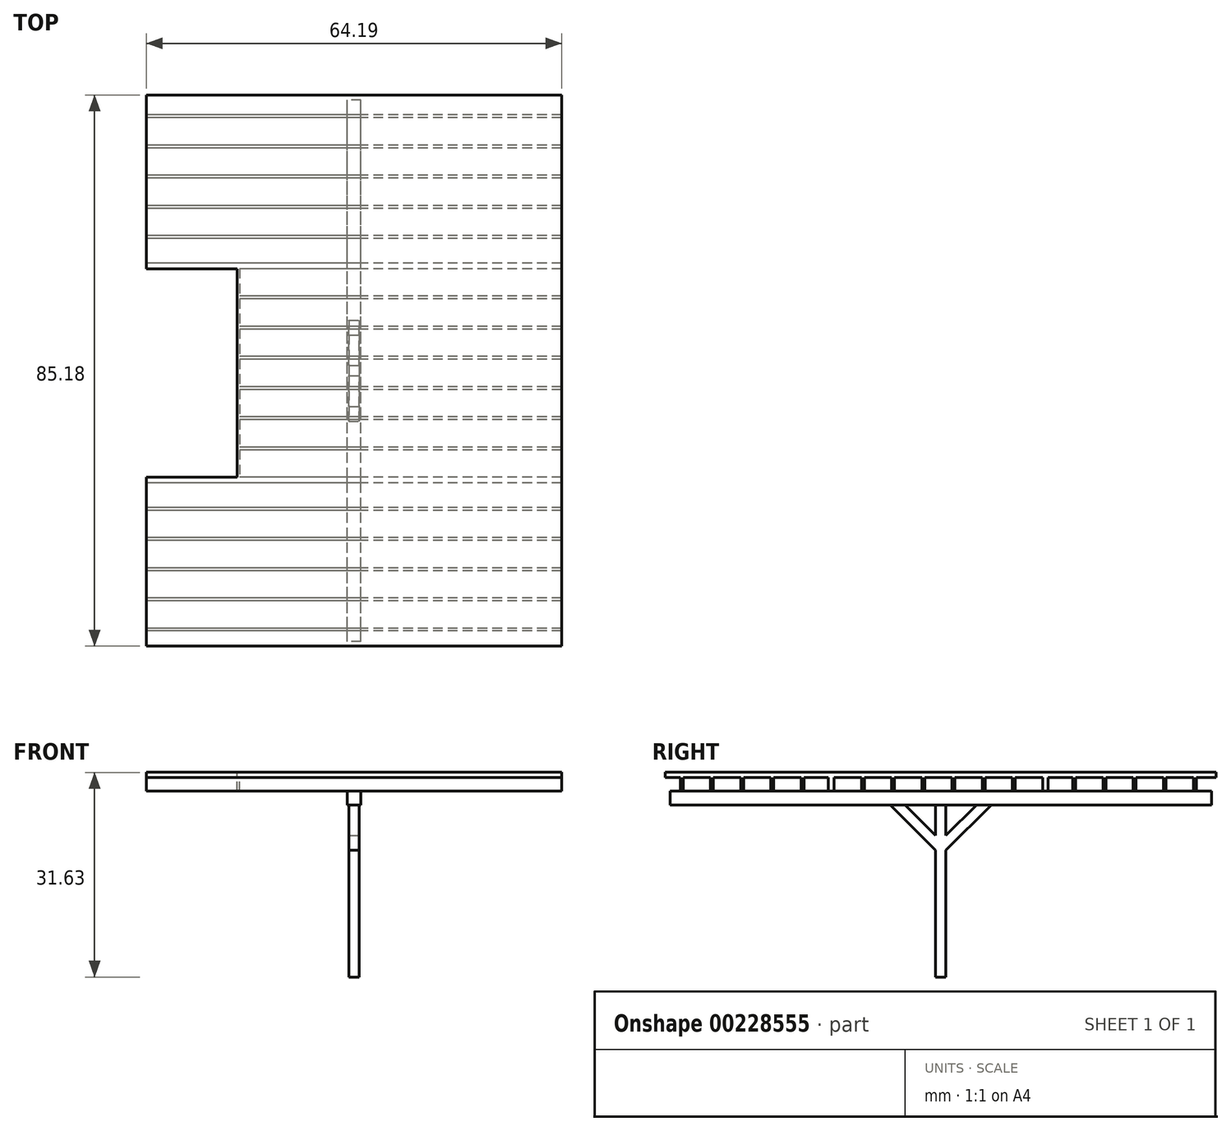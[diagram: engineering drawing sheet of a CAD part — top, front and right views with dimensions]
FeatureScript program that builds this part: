
annotation { "Feature Type Name" : "Feature", "Feature Type Description" : "" }
export const myFeature = defineFeature(function(context is Context, id is Id, definition is map)
    precondition{}
    {
        {
            var Q0;
            Q0=qCreatedBy(makeId("Top.planeOp"),FACE);
            var sketch = newSketch(context, id + "F0", { "sketchPlane" : qUnion([Q0])});
            skLineSegment(sketch, "E0.bottom", {"start": v(-4.2, 0) * mm, "end": v(5863.2, 0) * mm});
            skLineSegment(sketch, "E0.top", {"start": v(-4.2, -7696.2) * mm, "end": v(5863.2, -7696.2) * mm});
            skLineSegment(sketch, "E0.left", {"start": v(-4.2, 0) * mm, "end": v(-4.2, -7696.2) * mm});
            skLineSegment(sketch, "E0.right", {"start": v(5863.2, 0) * mm, "end": v(5863.2, -7696.2) * mm});
            skSolve(sketch);
        }
        {
            var Q0;
            Q0=makeQuery(id+"F0.imprint","IMPRINT",FACE,{"disambiguationData":[TD([[makeQuery(id+"F0.imprint","IMPRINT",EDGE,{"derivedFrom":sQuery(id+"F0.wireOp",EDGE,"E0.bottom")}),-1.0]])]});
            extrude(context, id + "F1", {"entities" : qUnion([Q0]), "depth" : 69.14 * mm});
        }
        {
            var Q0;
            Q0=makeQuery(id+"F1.opExtrude","CAP_FACE",FACE,{"disambiguationData":[OSD([sQuery(id+"F0.wireOp",EDGE,"E0.bottom"),sQuery(id+"F0.wireOp",EDGE,"E0.top"),sQuery(id+"F0.wireOp",EDGE,"E0.left"),sQuery(id+"F0.wireOp",EDGE,"E0.right")])],"isStart":true});
            var sketch = newSketch(context, id + "F2", { "sketchPlane" : qUnion([Q0])});
            skLineSegment(sketch, "E1.0", {"start": v(33.9, 7658.1) * mm, "end": v(5825.1, 7658.1) * mm});
            skLineSegment(sketch, "E1.1", {"start": v(33.9, 38.1) * mm, "end": v(33.9, 7658.1) * mm});
            skLineSegment(sketch, "E1.2", {"start": v(33.9, 38.1) * mm, "end": v(5825.1, 38.1) * mm});
            skLineSegment(sketch, "E1.3", {"start": v(5825.1, 38.1) * mm, "end": v(5825.1, 7658.1) * mm});
            skSolve(sketch);
        }
        {
            var Q0;
            Q0=makeQuery(id+"F2.imprint","IMPRINT",FACE,{"disambiguationData":[TD([[makeQuery(id+"F2.imprint","IMPRINT",EDGE,{"derivedFrom":sQuery(id+"F2.wireOp",EDGE,"E1.0")}),1.0]])]});
            extrude(context, id + "F3", {"entities" : qUnion([Q0]), "operationType" : NewBodyOperationType.ADD, "depth" : 184.15 * mm});
        }
        {
            var Q0;
            Q0=qCreatedBy(makeId("Right.planeOp"),FACE);
            var sketch = newSketch(context, id + "F4", { "sketchPlane" : qUnion([Q0])});
            skLineSegment(sketch, "E2.bottom", {"start": v(-406.4, 0) * mm, "end": v(-444.5, 0) * mm});
            skLineSegment(sketch, "E2.top", {"start": v(-406.4, -184.15) * mm, "end": v(-444.5, -184.15) * mm});
            skLineSegment(sketch, "E2.left", {"start": v(-406.4, 0) * mm, "end": v(-406.4, -184.15) * mm});
            skLineSegment(sketch, "E2.right", {"start": v(-444.5, 0) * mm, "end": v(-444.5, -184.15) * mm});
            skLineSegment(sketch, "E3.1.0.0", {"start": v(-812.8, 0) * mm, "end": v(-812.8, -184.15) * mm});
            skLineSegment(sketch, "E3.1.0.1", {"start": v(-850.9, 0) * mm, "end": v(-850.9, -184.15) * mm});
            skLineSegment(sketch, "E3.1.0.2", {"start": v(-812.8, 0) * mm, "end": v(-850.9, 0) * mm});
            skLineSegment(sketch, "E3.1.0.3", {"start": v(-812.8, -184.15) * mm, "end": v(-850.9, -184.15) * mm});
            skLineSegment(sketch, "E3.2.0.0", {"start": v(-1219.2, 0) * mm, "end": v(-1219.2, -184.15) * mm});
            skLineSegment(sketch, "E3.2.0.1", {"start": v(-1257.3, 0) * mm, "end": v(-1257.3, -184.15) * mm});
            skLineSegment(sketch, "E3.2.0.2", {"start": v(-1219.2, 0) * mm, "end": v(-1257.3, 0) * mm});
            skLineSegment(sketch, "E3.2.0.3", {"start": v(-1219.2, -184.15) * mm, "end": v(-1257.3, -184.15) * mm});
            skLineSegment(sketch, "E3.3.0.0", {"start": v(-1625.6, 0) * mm, "end": v(-1625.6, -184.15) * mm});
            skLineSegment(sketch, "E3.3.0.1", {"start": v(-1663.7, 0) * mm, "end": v(-1663.7, -184.15) * mm});
            skLineSegment(sketch, "E3.3.0.2", {"start": v(-1625.6, 0) * mm, "end": v(-1663.7, 0) * mm});
            skLineSegment(sketch, "E3.3.0.3", {"start": v(-1625.6, -184.15) * mm, "end": v(-1663.7, -184.15) * mm});
            skLineSegment(sketch, "E3.4.0.0", {"start": v(-2032, 0) * mm, "end": v(-2032, -184.15) * mm});
            skLineSegment(sketch, "E3.4.0.1", {"start": v(-2070.1, 0) * mm, "end": v(-2070.1, -184.15) * mm});
            skLineSegment(sketch, "E3.4.0.2", {"start": v(-2032, 0) * mm, "end": v(-2070.1, 0) * mm});
            skLineSegment(sketch, "E3.4.0.3", {"start": v(-2032, -184.15) * mm, "end": v(-2070.1, -184.15) * mm});
            skLineSegment(sketch, "E3.5.0.0", {"start": v(-2438.4, 0) * mm, "end": v(-2438.4, -184.15) * mm});
            skLineSegment(sketch, "E3.5.0.1", {"start": v(-2476.5, 0) * mm, "end": v(-2476.5, -184.15) * mm});
            skLineSegment(sketch, "E3.5.0.2", {"start": v(-2438.4, 0) * mm, "end": v(-2476.5, 0) * mm});
            skLineSegment(sketch, "E3.5.0.3", {"start": v(-2438.4, -184.15) * mm, "end": v(-2476.5, -184.15) * mm});
            skLineSegment(sketch, "E3.6.0.0", {"start": v(-2844.8, 0) * mm, "end": v(-2844.8, -184.15) * mm});
            skLineSegment(sketch, "E3.6.0.1", {"start": v(-2882.9, 0) * mm, "end": v(-2882.9, -184.15) * mm});
            skLineSegment(sketch, "E3.6.0.2", {"start": v(-2844.8, 0) * mm, "end": v(-2882.9, 0) * mm});
            skLineSegment(sketch, "E3.6.0.3", {"start": v(-2844.8, -184.15) * mm, "end": v(-2882.9, -184.15) * mm});
            skLineSegment(sketch, "E3.7.0.0", {"start": v(-3251.2, 0) * mm, "end": v(-3251.2, -184.15) * mm});
            skLineSegment(sketch, "E3.7.0.1", {"start": v(-3289.3, 0) * mm, "end": v(-3289.3, -184.15) * mm});
            skLineSegment(sketch, "E3.7.0.2", {"start": v(-3251.2, 0) * mm, "end": v(-3289.3, 0) * mm});
            skLineSegment(sketch, "E3.7.0.3", {"start": v(-3251.2, -184.15) * mm, "end": v(-3289.3, -184.15) * mm});
            skLineSegment(sketch, "E3.8.0.0", {"start": v(-3657.6, 0) * mm, "end": v(-3657.6, -184.15) * mm});
            skLineSegment(sketch, "E3.8.0.1", {"start": v(-3695.7, 0) * mm, "end": v(-3695.7, -184.15) * mm});
            skLineSegment(sketch, "E3.8.0.2", {"start": v(-3657.6, 0) * mm, "end": v(-3695.7, 0) * mm});
            skLineSegment(sketch, "E3.8.0.3", {"start": v(-3657.6, -184.15) * mm, "end": v(-3695.7, -184.15) * mm});
            skLineSegment(sketch, "E3.9.0.0", {"start": v(-4064, 0) * mm, "end": v(-4064, -184.15) * mm});
            skLineSegment(sketch, "E3.9.0.1", {"start": v(-4102.1, 0) * mm, "end": v(-4102.1, -184.15) * mm});
            skLineSegment(sketch, "E3.9.0.2", {"start": v(-4064, 0) * mm, "end": v(-4102.1, 0) * mm});
            skLineSegment(sketch, "E3.9.0.3", {"start": v(-4064, -184.15) * mm, "end": v(-4102.1, -184.15) * mm});
            skLineSegment(sketch, "E3.10.0.0", {"start": v(-4470.4, 0) * mm, "end": v(-4470.4, -184.15) * mm});
            skLineSegment(sketch, "E3.10.0.1", {"start": v(-4508.5, 0) * mm, "end": v(-4508.5, -184.15) * mm});
            skLineSegment(sketch, "E3.10.0.2", {"start": v(-4470.4, 0) * mm, "end": v(-4508.5, 0) * mm});
            skLineSegment(sketch, "E3.10.0.3", {"start": v(-4470.4, -184.15) * mm, "end": v(-4508.5, -184.15) * mm});
            skLineSegment(sketch, "E3.11.0.0", {"start": v(-4876.8, 0) * mm, "end": v(-4876.8, -184.15) * mm});
            skLineSegment(sketch, "E3.11.0.1", {"start": v(-4914.9, 0) * mm, "end": v(-4914.9, -184.15) * mm});
            skLineSegment(sketch, "E3.11.0.2", {"start": v(-4876.8, 0) * mm, "end": v(-4914.9, 0) * mm});
            skLineSegment(sketch, "E3.11.0.3", {"start": v(-4876.8, -184.15) * mm, "end": v(-4914.9, -184.15) * mm});
            skLineSegment(sketch, "E3.12.0.0", {"start": v(-5283.2, 0) * mm, "end": v(-5283.2, -184.15) * mm});
            skLineSegment(sketch, "E3.12.0.1", {"start": v(-5321.3, 0) * mm, "end": v(-5321.3, -184.15) * mm});
            skLineSegment(sketch, "E3.12.0.2", {"start": v(-5283.2, 0) * mm, "end": v(-5321.3, 0) * mm});
            skLineSegment(sketch, "E3.12.0.3", {"start": v(-5283.2, -184.15) * mm, "end": v(-5321.3, -184.15) * mm});
            skLineSegment(sketch, "E3.13.0.0", {"start": v(-5689.6, 0) * mm, "end": v(-5689.6, -184.15) * mm});
            skLineSegment(sketch, "E3.13.0.1", {"start": v(-5727.7, 0) * mm, "end": v(-5727.7, -184.15) * mm});
            skLineSegment(sketch, "E3.13.0.2", {"start": v(-5689.6, 0) * mm, "end": v(-5727.7, 0) * mm});
            skLineSegment(sketch, "E3.13.0.3", {"start": v(-5689.6, -184.15) * mm, "end": v(-5727.7, -184.15) * mm});
            skLineSegment(sketch, "E3.14.0.0", {"start": v(-6096, 0) * mm, "end": v(-6096, -184.15) * mm});
            skLineSegment(sketch, "E3.14.0.1", {"start": v(-6134.1, 0) * mm, "end": v(-6134.1, -184.15) * mm});
            skLineSegment(sketch, "E3.14.0.2", {"start": v(-6096, 0) * mm, "end": v(-6134.1, 0) * mm});
            skLineSegment(sketch, "E3.14.0.3", {"start": v(-6096, -184.15) * mm, "end": v(-6134.1, -184.15) * mm});
            skLineSegment(sketch, "E3.15.0.0", {"start": v(-6502.4, 0) * mm, "end": v(-6502.4, -184.15) * mm});
            skLineSegment(sketch, "E3.15.0.1", {"start": v(-6540.5, 0) * mm, "end": v(-6540.5, -184.15) * mm});
            skLineSegment(sketch, "E3.15.0.2", {"start": v(-6502.4, 0) * mm, "end": v(-6540.5, 0) * mm});
            skLineSegment(sketch, "E3.15.0.3", {"start": v(-6502.4, -184.15) * mm, "end": v(-6540.5, -184.15) * mm});
            skLineSegment(sketch, "E3.16.0.0", {"start": v(-6908.8, 0) * mm, "end": v(-6908.8, -184.15) * mm});
            skLineSegment(sketch, "E3.16.0.1", {"start": v(-6946.9, 0) * mm, "end": v(-6946.9, -184.15) * mm});
            skLineSegment(sketch, "E3.16.0.2", {"start": v(-6908.8, 0) * mm, "end": v(-6946.9, 0) * mm});
            skLineSegment(sketch, "E3.16.0.3", {"start": v(-6908.8, -184.15) * mm, "end": v(-6946.9, -184.15) * mm});
            skLineSegment(sketch, "E3.direction1", {"start": v(-444.5, -184.15) * mm, "end": v(-850.9, -184.15) * mm, "construction": true});
            skLineSegment(sketch, "E4.0.17.0", {"start": v(-7315.2, 0) * mm, "end": v(-7315.2, -184.15) * mm});
            skLineSegment(sketch, "E4.3.17.0", {"start": v(-7353.3, 0) * mm, "end": v(-7353.3, -184.15) * mm});
            skLineSegment(sketch, "E4.6.17.0", {"start": v(-7315.2, 0) * mm, "end": v(-7353.3, 0) * mm});
            skLineSegment(sketch, "E4.9.17.0", {"start": v(-7315.2, -184.15) * mm, "end": v(-7353.3, -184.15) * mm});
            skSolve(sketch);
        }
        {
            var Q0;
            Q0=makeQuery(id+"F4.imprint","IMPRINT",FACE,{"disambiguationData":[TD([[makeQuery(id+"F4.imprint","IMPRINT",EDGE,{"derivedFrom":sQuery(id+"F4.wireOp",EDGE,"E2.bottom")}),1.0]])]});
            var Q1;
            Q1=makeQuery(id+"F4.imprint","IMPRINT",FACE,{"disambiguationData":[TD([[makeQuery(id+"F4.imprint","IMPRINT",EDGE,{"derivedFrom":sQuery(id+"F4.wireOp",EDGE,"E3.1.0.0")}),-1.0]])]});
            var Q2;
            Q2=makeQuery(id+"F4.imprint","IMPRINT",FACE,{"disambiguationData":[TD([[makeQuery(id+"F4.imprint","IMPRINT",EDGE,{"derivedFrom":sQuery(id+"F4.wireOp",EDGE,"E3.2.0.0")}),-1.0]])]});
            var Q3;
            Q3=makeQuery(id+"F4.imprint","IMPRINT",FACE,{"disambiguationData":[TD([[makeQuery(id+"F4.imprint","IMPRINT",EDGE,{"derivedFrom":sQuery(id+"F4.wireOp",EDGE,"E3.3.0.0")}),-1.0]])]});
            var Q4;
            Q4=makeQuery(id+"F4.imprint","IMPRINT",FACE,{"disambiguationData":[TD([[makeQuery(id+"F4.imprint","IMPRINT",EDGE,{"derivedFrom":sQuery(id+"F4.wireOp",EDGE,"E3.4.0.0")}),-1.0]])]});
            var Q5;
            Q5=makeQuery(id+"F4.imprint","IMPRINT",FACE,{"disambiguationData":[TD([[makeQuery(id+"F4.imprint","IMPRINT",EDGE,{"derivedFrom":sQuery(id+"F4.wireOp",EDGE,"E3.5.0.0")}),-1.0]])]});
            var Q6;
            Q6=makeQuery(id+"F4.imprint","IMPRINT",FACE,{"disambiguationData":[TD([[makeQuery(id+"F4.imprint","IMPRINT",EDGE,{"derivedFrom":sQuery(id+"F4.wireOp",EDGE,"E3.6.0.0")}),-1.0]])]});
            var Q7;
            Q7=makeQuery(id+"F4.imprint","IMPRINT",FACE,{"disambiguationData":[TD([[makeQuery(id+"F4.imprint","IMPRINT",EDGE,{"derivedFrom":sQuery(id+"F4.wireOp",EDGE,"E3.7.0.0")}),-1.0]])]});
            var Q8;
            Q8=makeQuery(id+"F4.imprint","IMPRINT",FACE,{"disambiguationData":[TD([[makeQuery(id+"F4.imprint","IMPRINT",EDGE,{"derivedFrom":sQuery(id+"F4.wireOp",EDGE,"E3.8.0.0")}),-1.0]])]});
            var Q9;
            Q9=makeQuery(id+"F4.imprint","IMPRINT",FACE,{"disambiguationData":[TD([[makeQuery(id+"F4.imprint","IMPRINT",EDGE,{"derivedFrom":sQuery(id+"F4.wireOp",EDGE,"E3.9.0.0")}),-1.0]])]});
            var Q10;
            Q10=makeQuery(id+"F4.imprint","IMPRINT",FACE,{"disambiguationData":[TD([[makeQuery(id+"F4.imprint","IMPRINT",EDGE,{"derivedFrom":sQuery(id+"F4.wireOp",EDGE,"E3.10.0.0")}),-1.0]])]});
            var Q11;
            Q11=makeQuery(id+"F4.imprint","IMPRINT",FACE,{"disambiguationData":[TD([[makeQuery(id+"F4.imprint","IMPRINT",EDGE,{"derivedFrom":sQuery(id+"F4.wireOp",EDGE,"E3.11.0.0")}),-1.0]])]});
            var Q12;
            Q12=makeQuery(id+"F4.imprint","IMPRINT",FACE,{"disambiguationData":[TD([[makeQuery(id+"F4.imprint","IMPRINT",EDGE,{"derivedFrom":sQuery(id+"F4.wireOp",EDGE,"E3.12.0.0")}),-1.0]])]});
            var Q13;
            Q13=makeQuery(id+"F4.imprint","IMPRINT",FACE,{"disambiguationData":[TD([[makeQuery(id+"F4.imprint","IMPRINT",EDGE,{"derivedFrom":sQuery(id+"F4.wireOp",EDGE,"E3.13.0.0")}),-1.0]])]});
            var Q14;
            Q14=makeQuery(id+"F4.imprint","IMPRINT",FACE,{"disambiguationData":[TD([[makeQuery(id+"F4.imprint","IMPRINT",EDGE,{"derivedFrom":sQuery(id+"F4.wireOp",EDGE,"E3.14.0.0")}),-1.0]])]});
            var Q15;
            Q15=makeQuery(id+"F4.imprint","IMPRINT",FACE,{"disambiguationData":[TD([[makeQuery(id+"F4.imprint","IMPRINT",EDGE,{"derivedFrom":sQuery(id+"F4.wireOp",EDGE,"E3.15.0.0")}),-1.0]])]});
            var Q16;
            Q16=makeQuery(id+"F4.imprint","IMPRINT",FACE,{"disambiguationData":[TD([[makeQuery(id+"F4.imprint","IMPRINT",EDGE,{"derivedFrom":sQuery(id+"F4.wireOp",EDGE,"E3.16.0.0")}),-1.0]])]});
            var Q17;
            Q17=makeQuery(id+"F4.imprint","IMPRINT",FACE,{"disambiguationData":[TD([[makeQuery(id+"F4.imprint","IMPRINT",EDGE,{"derivedFrom":sQuery(id+"F4.wireOp",EDGE,"E4.0.17.0")}),-1.0]])]});
            var Q18;
            Q18=makeQuery(id+"F1.opExtrude","SWEPT_FACE",FACE,{"disambiguationData":[OSD([sQuery(id+"F0.wireOp",EDGE,"E0.right")])]});
            extrude(context, id + "F5", {"entities" : qUnion([Q0, Q1, Q2, Q3, Q4, Q5, Q6, Q7, Q8, Q9, Q10, Q11, Q12, Q13, Q14, Q15, Q16, Q17]), "operationType" : NewBodyOperationType.ADD, "endBound" : BoundingType.UP_TO_SURFACE, "endBoundEntityFace" : qUnion([Q18]), "depth" : 25.4 * mm});
        }
        {
            var Q0;
            {var subQ0=sQuery(id+"F0.wireOp",EDGE,"E0.bottom");Q0=makeQuery(id+"F3.boolean.opBoolean","MERGE",FACE,{"derivedFrom":[makeQuery(id+"F1.opExtrude","SWEPT_FACE",FACE,{"disambiguationData":[OSD([subQ0])]}),makeQuery(id+"F3.opExtrude","SWEPT_FACE",FACE,{"disambiguationData":[OSD([subQ0])]})]});}
            cPlane(context, id + "F6", {"entities" : qUnion([Q0]), "cplaneType" : CPlaneType.OFFSET, "offset" : 203.2 * mm, "oppositeDirection" : true, "width" : 152.4 * mm, "height" : 152.4 * mm});
        }
        {
            var Q0;
            Q0=qCreatedBy(id+"F6.planeOp",FACE);
            var sketch = newSketch(context, id + "F7", { "sketchPlane" : qUnion([Q0])});
            skLineSegment(sketch, "E5.bottom", {"start": v(-3021.58, -184.15) * mm, "end": v(-2837.43, -184.15) * mm});
            skLineSegment(sketch, "E5.top", {"start": v(-3021.58, -368.3) * mm, "end": v(-2837.43, -368.3) * mm});
            skLineSegment(sketch, "E5.left", {"start": v(-3021.58, -184.15) * mm, "end": v(-3021.58, -368.3) * mm});
            skLineSegment(sketch, "E5.right", {"start": v(-2837.43, -184.15) * mm, "end": v(-2837.43, -368.3) * mm});
            skSolve(sketch);
        }
        {
            var Q0;
            Q0=makeQuery(id+"F7.imprint","IMPRINT",FACE,{"disambiguationData":[TD([[makeQuery(id+"F7.imprint","IMPRINT",EDGE,{"derivedFrom":sQuery(id+"F7.wireOp",EDGE,"E5.bottom")}),-1.0]])]});
            extrude(context, id + "F8", {"entities" : qUnion([Q0]), "operationType" : NewBodyOperationType.ADD, "oppositeDirection" : true, "depth" : 7289.8 * mm});
        }
        {
            var Q0;
            Q0=makeQuery(id+"F8.opExtrude","SWEPT_FACE",FACE,{"disambiguationData":[OSD([sQuery(id+"F7.wireOp",EDGE,"E5.top")])]});
            var sketch = newSketch(context, id + "F9", { "sketchPlane" : qUnion([Q0])});
            skLineSegment(sketch, "E6", {"start": v(2929.5, 7493) * mm, "end": v(2929.5, 203.2) * mm, "construction": true});
            skLineSegment(sketch, "E7", {"start": v(2837.43, 3848.1) * mm, "end": v(3021.58, 3848.1) * mm, "construction": true});
            skLineSegment(sketch, "E8.bottom", {"start": v(2999.36, 3778.25) * mm, "end": v(2859.66, 3778.25) * mm});
            skLineSegment(sketch, "E8.top", {"start": v(2999.36, 3917.95) * mm, "end": v(2859.66, 3917.95) * mm});
            skLineSegment(sketch, "E8.left", {"start": v(2999.36, 3778.25) * mm, "end": v(2999.36, 3917.95) * mm});
            skLineSegment(sketch, "E8.right", {"start": v(2859.66, 3778.25) * mm, "end": v(2859.66, 3917.95) * mm});
            skPoint(sketch, "E8.middle", {"position": v(2929.5, 3848.1) * mm});
            skSolve(sketch);
        }
        {
            var Q0;
            Q0=makeQuery(id+"F9.imprint","IMPRINT",FACE,{"disambiguationData":[TD([[makeQuery(id+"F9.imprint","IMPRINT",EDGE,{"derivedFrom":sQuery(id+"F9.wireOp",EDGE,"E8.bottom")}),-1.0]])]});
            extrude(context, id + "F10", {"entities" : qUnion([Q0]), "operationType" : NewBodyOperationType.ADD, "depth" : 2317.62 * mm});
        }
        {
            var Q0;
            Q0=makeQuery(id+"F10.opExtrude","SWEPT_FACE",FACE,{"disambiguationData":[OSD([sQuery(id+"F9.wireOp",EDGE,"E8.left")])]});
            var sketch = newSketch(context, id + "F11", { "sketchPlane" : qUnion([Q0])});
            skLineSegment(sketch, "E9", {"start": v(-4329.98, -368.3) * mm, "end": v(-3917.95, -780.33) * mm});
            skLineSegment(sketch, "E10", {"start": v(-3917.95, -780.33) * mm, "end": v(-3917.95, -977.9) * mm});
            skLineSegment(sketch, "E11", {"start": v(-3917.95, -977.9) * mm, "end": v(-4527.55, -368.3) * mm});
            skLineSegment(sketch, "E12", {"start": v(-4527.55, -368.3) * mm, "end": v(-4329.98, -368.3) * mm});
            skLineSegment(sketch, "E13", {"start": v(-3848.1, -1904.76) * mm, "end": v(-3848.1, -2685.92) * mm, "construction": true});
            skLineSegment(sketch, "E14.MirrorCS", {"start": v(-3168.65, -368.3) * mm, "end": v(-3366.22, -368.3) * mm});
            skLineSegment(sketch, "E15.MirrorCS", {"start": v(-3778.25, -977.9) * mm, "end": v(-3168.65, -368.3) * mm});
            skLineSegment(sketch, "E16.MirrorCS", {"start": v(-3366.22, -368.3) * mm, "end": v(-3778.25, -780.33) * mm});
            skLineSegment(sketch, "E17.MirrorCS", {"start": v(-3778.25, -780.33) * mm, "end": v(-3778.25, -977.9) * mm});
            skSolve(sketch);
        }
        {
            var Q0;
            Q0=makeQuery(id+"F11.imprint","IMPRINT",FACE,{"disambiguationData":[TD([[makeQuery(id+"F11.imprint","IMPRINT",EDGE,{"derivedFrom":sQuery(id+"F11.wireOp",EDGE,"E9")}),-1.0]])]});
            var Q1;
            Q1=makeQuery(id+"F11.imprint","IMPRINT",FACE,{"disambiguationData":[TD([[makeQuery(id+"F11.imprint","IMPRINT",EDGE,{"derivedFrom":sQuery(id+"F11.wireOp",EDGE,"E14.MirrorCS")}),1.0]])]});
            var Q2;
            Q2=makeQuery(id+"F11.imprint","IMPRINT",FACE,{"disambiguationData":[TD([[makeQuery(id+"F11.imprint","IMPRINT",EDGE,{"derivedFrom":sQuery(id+"F11.wireOp",EDGE,"E14.MirrorCS")}),-1.0]])]});
            var Q3;
            Q3=makeQuery(id+"F10.opExtrude","SWEPT_FACE",FACE,{"disambiguationData":[OSD([sQuery(id+"F9.wireOp",EDGE,"E8.right")])]});
            extrude(context, id + "F12", {"entities" : qUnion([Q0, Q1, Q2]), "operationType" : NewBodyOperationType.ADD, "endBound" : BoundingType.UP_TO_SURFACE, "oppositeDirection" : true, "endBoundEntityFace" : qUnion([Q3]), "depth" : 25.4 * mm});
        }
        {
            var Q0;
            Q0=makeQuery(id+"F1.opExtrude","CAP_FACE",FACE,{"disambiguationData":[OSD([sQuery(id+"F0.wireOp",EDGE,"E0.bottom"),sQuery(id+"F0.wireOp",EDGE,"E0.top"),sQuery(id+"F0.wireOp",EDGE,"E0.left"),sQuery(id+"F0.wireOp",EDGE,"E0.right")])],"isStart":false});
            var sketch = newSketch(context, id + "F13", { "sketchPlane" : qUnion([Q0])});
            skLineSegment(sketch, "E18.0", {"start": v(134.08, -138.28) * mm, "end": v(5724.93, -138.28) * mm});
            skLineSegment(sketch, "E18.1", {"start": v(134.08, -138.28) * mm, "end": v(134.08, -7557.92) * mm});
            skLineSegment(sketch, "E18.2", {"start": v(134.08, -7557.92) * mm, "end": v(5724.93, -7557.92) * mm});
            skLineSegment(sketch, "E18.3", {"start": v(5724.93, -138.28) * mm, "end": v(5724.93, -7557.92) * mm});
            skLineSegment(sketch, "E19.0", {"start": v(-4.2, 0) * mm, "end": v(5863.2, 0) * mm});
            skLineSegment(sketch, "E20.0", {"start": v(-4.2, 0) * mm, "end": v(-4.2, -7696.2) * mm});
            skLineSegment(sketch, "E21.0", {"start": v(-4.2, -7696.2) * mm, "end": v(5863.2, -7696.2) * mm});
            skLineSegment(sketch, "E22.0", {"start": v(5863.2, 0) * mm, "end": v(5863.2, -7696.2) * mm});
            skSolve(sketch);
        }
        {
            var Q0;
            Q0=makeQuery(id+"F13.imprint","IMPRINT",FACE,{"disambiguationData":[TD([[makeQuery(id+"F13.imprint","IMPRINT",EDGE,{"derivedFrom":sQuery(id+"F13.wireOp",EDGE,"E18.0")}),1.0]])]});
            var Q1;
            Q1=makeQuery(id+"F5.boolean.opBoolean","MERGE",FACE,{"derivedFrom":[makeQuery(id+"F3.opExtrude","CAP_FACE",FACE,{"disambiguationData":[OSD([sQuery(id+"F0.wireOp",EDGE,"E0.bottom"),sQuery(id+"F0.wireOp",EDGE,"E0.top"),sQuery(id+"F0.wireOp",EDGE,"E0.left"),sQuery(id+"F0.wireOp",EDGE,"E0.right"),sQuery(id+"F2.wireOp",EDGE,"E1.0"),sQuery(id+"F2.wireOp",EDGE,"E1.1"),sQuery(id+"F2.wireOp",EDGE,"E1.2"),sQuery(id+"F2.wireOp",EDGE,"E1.3")])],"isStart":false}),makeQuery(id+"F5.opExtrude","SWEPT_FACE",FACE,{"disambiguationData":[OSD([sQuery(id+"F4.wireOp",EDGE,"E2.top")])]}),makeQuery(id+"F5.opExtrude","SWEPT_FACE",FACE,{"disambiguationData":[OSD([sQuery(id+"F4.wireOp",EDGE,"E3.1.0.3")])]}),makeQuery(id+"F5.opExtrude","SWEPT_FACE",FACE,{"disambiguationData":[OSD([sQuery(id+"F4.wireOp",EDGE,"E3.2.0.3")])]}),makeQuery(id+"F5.opExtrude","SWEPT_FACE",FACE,{"disambiguationData":[OSD([sQuery(id+"F4.wireOp",EDGE,"E3.3.0.3")])]}),makeQuery(id+"F5.opExtrude","SWEPT_FACE",FACE,{"disambiguationData":[OSD([sQuery(id+"F4.wireOp",EDGE,"E3.4.0.3")])]}),makeQuery(id+"F5.opExtrude","SWEPT_FACE",FACE,{"disambiguationData":[OSD([sQuery(id+"F4.wireOp",EDGE,"E3.5.0.3")])]}),makeQuery(id+"F5.opExtrude","SWEPT_FACE",FACE,{"disambiguationData":[OSD([sQuery(id+"F4.wireOp",EDGE,"E3.6.0.3")])]}),makeQuery(id+"F5.opExtrude","SWEPT_FACE",FACE,{"disambiguationData":[OSD([sQuery(id+"F4.wireOp",EDGE,"E3.7.0.3")])]}),makeQuery(id+"F5.opExtrude","SWEPT_FACE",FACE,{"disambiguationData":[OSD([sQuery(id+"F4.wireOp",EDGE,"E3.8.0.3")])]}),makeQuery(id+"F5.opExtrude","SWEPT_FACE",FACE,{"disambiguationData":[OSD([sQuery(id+"F4.wireOp",EDGE,"E3.9.0.3")])]}),makeQuery(id+"F5.opExtrude","SWEPT_FACE",FACE,{"disambiguationData":[OSD([sQuery(id+"F4.wireOp",EDGE,"E3.10.0.3")])]}),makeQuery(id+"F5.opExtrude","SWEPT_FACE",FACE,{"disambiguationData":[OSD([sQuery(id+"F4.wireOp",EDGE,"E3.11.0.3")])]}),makeQuery(id+"F5.opExtrude","SWEPT_FACE",FACE,{"disambiguationData":[OSD([sQuery(id+"F4.wireOp",EDGE,"E3.12.0.3")])]}),makeQuery(id+"F5.opExtrude","SWEPT_FACE",FACE,{"disambiguationData":[OSD([sQuery(id+"F4.wireOp",EDGE,"E3.13.0.3")])]}),makeQuery(id+"F5.opExtrude","SWEPT_FACE",FACE,{"disambiguationData":[OSD([sQuery(id+"F4.wireOp",EDGE,"E3.14.0.3")])]}),makeQuery(id+"F5.opExtrude","SWEPT_FACE",FACE,{"disambiguationData":[OSD([sQuery(id+"F4.wireOp",EDGE,"E3.15.0.3")])]}),makeQuery(id+"F5.opExtrude","SWEPT_FACE",FACE,{"disambiguationData":[OSD([sQuery(id+"F4.wireOp",EDGE,"E3.16.0.3")])]}),makeQuery(id+"F5.opExtrude","SWEPT_FACE",FACE,{"disambiguationData":[OSD([sQuery(id+"F4.wireOp",EDGE,"E4.9.17.0")])]})]});
            extrude(context, id + "F14", {"entities" : qUnion([Q0]), "operationType" : NewBodyOperationType.REMOVE, "endBound" : BoundingType.UP_TO_SURFACE, "oppositeDirection" : true, "endBoundEntityFace" : qUnion([Q1]), "depth" : 25.4 * mm});
        }
        {
            var Q0;
            Q0=makeQuery(id+"F1.opExtrude","CAP_FACE",FACE,{"disambiguationData":[OSD([sQuery(id+"F0.wireOp",EDGE,"E0.bottom"),sQuery(id+"F0.wireOp",EDGE,"E0.top"),sQuery(id+"F0.wireOp",EDGE,"E0.left"),sQuery(id+"F0.wireOp",EDGE,"E0.right")])],"isStart":false});
            var sketch = newSketch(context, id + "F15", { "sketchPlane" : qUnion([Q0])});
            skLineSegment(sketch, "E23.bottom", {"start": v(134.08, -2476.5) * mm, "end": v(1353.28, -2476.5) * mm});
            skLineSegment(sketch, "E23.top", {"start": v(134.08, -5283.2) * mm, "end": v(1353.28, -5283.2) * mm});
            skLineSegment(sketch, "E23.left", {"start": v(134.08, -2476.5) * mm, "end": v(134.08, -5283.2) * mm});
            skLineSegment(sketch, "E23.right", {"start": v(1353.28, -2476.5) * mm, "end": v(1353.28, -5283.2) * mm});
            skSolve(sketch);
        }
        {
            var Q0;
            Q0=makeQuery(id+"F15.imprint","IMPRINT",FACE,{"disambiguationData":[TD([[makeQuery(id+"F15.imprint","IMPRINT",EDGE,{"derivedFrom":sQuery(id+"F15.wireOp",EDGE,"E23.bottom")}),-1.0]])]});
            var Q1;
            Q1=makeQuery(id+"F14.boolean.opBoolean","SPLIT",FACE,{"disambiguationData":[TD([makeQuery(id+"F5.opExtrude","SWEPT_FACE",FACE,{"disambiguationData":[OSD([sQuery(id+"F4.wireOp",EDGE,"E3.5.0.0")])]}),makeQuery(id+"F5.opExtrude","SWEPT_FACE",FACE,{"disambiguationData":[OSD([sQuery(id+"F4.wireOp",EDGE,"E3.5.0.1")])]}),makeQuery(id+"F8.opExtrude","SWEPT_FACE",FACE,{"disambiguationData":[OSD([sQuery(id+"F7.wireOp",EDGE,"E5.bottom")])]}),makeQuery(id+"F8.opExtrude","SWEPT_FACE",FACE,{"disambiguationData":[OSD([sQuery(id+"F7.wireOp",EDGE,"E5.right")])]}),makeQuery(id+"F14.opExtrude","SWEPT_FACE",FACE,{"disambiguationData":[OSD([sQuery(id+"F13.wireOp",EDGE,"E18.1")])]})])],"derivedFrom":makeQuery(id+"F5.boolean.opBoolean","MERGE",FACE,{"derivedFrom":[makeQuery(id+"F3.opExtrude","CAP_FACE",FACE,{"disambiguationData":[OSD([sQuery(id+"F0.wireOp",EDGE,"E0.bottom"),sQuery(id+"F0.wireOp",EDGE,"E0.top"),sQuery(id+"F0.wireOp",EDGE,"E0.left"),sQuery(id+"F0.wireOp",EDGE,"E0.right"),sQuery(id+"F2.wireOp",EDGE,"E1.0"),sQuery(id+"F2.wireOp",EDGE,"E1.1"),sQuery(id+"F2.wireOp",EDGE,"E1.2"),sQuery(id+"F2.wireOp",EDGE,"E1.3")])],"isStart":false}),makeQuery(id+"F5.opExtrude","SWEPT_FACE",FACE,{"disambiguationData":[OSD([sQuery(id+"F4.wireOp",EDGE,"E2.top")])]}),makeQuery(id+"F5.opExtrude","SWEPT_FACE",FACE,{"disambiguationData":[OSD([sQuery(id+"F4.wireOp",EDGE,"E3.1.0.3")])]}),makeQuery(id+"F5.opExtrude","SWEPT_FACE",FACE,{"disambiguationData":[OSD([sQuery(id+"F4.wireOp",EDGE,"E3.2.0.3")])]}),makeQuery(id+"F5.opExtrude","SWEPT_FACE",FACE,{"disambiguationData":[OSD([sQuery(id+"F4.wireOp",EDGE,"E3.3.0.3")])]}),makeQuery(id+"F5.opExtrude","SWEPT_FACE",FACE,{"disambiguationData":[OSD([sQuery(id+"F4.wireOp",EDGE,"E3.4.0.3")])]}),makeQuery(id+"F5.opExtrude","SWEPT_FACE",FACE,{"disambiguationData":[OSD([sQuery(id+"F4.wireOp",EDGE,"E3.5.0.3")])]}),makeQuery(id+"F5.opExtrude","SWEPT_FACE",FACE,{"disambiguationData":[OSD([sQuery(id+"F4.wireOp",EDGE,"E3.6.0.3")])]}),makeQuery(id+"F5.opExtrude","SWEPT_FACE",FACE,{"disambiguationData":[OSD([sQuery(id+"F4.wireOp",EDGE,"E3.7.0.3")])]}),makeQuery(id+"F5.opExtrude","SWEPT_FACE",FACE,{"disambiguationData":[OSD([sQuery(id+"F4.wireOp",EDGE,"E3.8.0.3")])]}),makeQuery(id+"F5.opExtrude","SWEPT_FACE",FACE,{"disambiguationData":[OSD([sQuery(id+"F4.wireOp",EDGE,"E3.9.0.3")])]}),makeQuery(id+"F5.opExtrude","SWEPT_FACE",FACE,{"disambiguationData":[OSD([sQuery(id+"F4.wireOp",EDGE,"E3.10.0.3")])]}),makeQuery(id+"F5.opExtrude","SWEPT_FACE",FACE,{"disambiguationData":[OSD([sQuery(id+"F4.wireOp",EDGE,"E3.11.0.3")])]}),makeQuery(id+"F5.opExtrude","SWEPT_FACE",FACE,{"disambiguationData":[OSD([sQuery(id+"F4.wireOp",EDGE,"E3.12.0.3")])]}),makeQuery(id+"F5.opExtrude","SWEPT_FACE",FACE,{"disambiguationData":[OSD([sQuery(id+"F4.wireOp",EDGE,"E3.13.0.3")])]}),makeQuery(id+"F5.opExtrude","SWEPT_FACE",FACE,{"disambiguationData":[OSD([sQuery(id+"F4.wireOp",EDGE,"E3.14.0.3")])]}),makeQuery(id+"F5.opExtrude","SWEPT_FACE",FACE,{"disambiguationData":[OSD([sQuery(id+"F4.wireOp",EDGE,"E3.15.0.3")])]}),makeQuery(id+"F5.opExtrude","SWEPT_FACE",FACE,{"disambiguationData":[OSD([sQuery(id+"F4.wireOp",EDGE,"E3.16.0.3")])]}),makeQuery(id+"F5.opExtrude","SWEPT_FACE",FACE,{"disambiguationData":[OSD([sQuery(id+"F4.wireOp",EDGE,"E4.9.17.0")])]})]})});
            extrude(context, id + "F16", {"entities" : qUnion([Q0]), "operationType" : NewBodyOperationType.REMOVE, "endBound" : BoundingType.UP_TO_SURFACE, "oppositeDirection" : true, "endBoundEntityFace" : qUnion([Q1]), "depth" : 25.4 * mm});
        }
        {
            var Q0;
            Q0=makeQuery(id+"F16.boolean.opBoolean","COPY",FACE,{"derivedFrom":makeQuery(id+"F16.opExtrude","SWEPT_FACE",FACE,{"disambiguationData":[OSD([sQuery(id+"F15.wireOp",EDGE,"E23.right")])]})});
            var sketch = newSketch(context, id + "F17", { "sketchPlane" : qUnion([Q0])});
            skLineSegment(sketch, "E24.bottom", {"start": v(2476.5, 69.14) * mm, "end": v(5283.2, 69.14) * mm});
            skLineSegment(sketch, "E24.top", {"start": v(2476.5, -184.15) * mm, "end": v(5283.2, -184.15) * mm});
            skLineSegment(sketch, "E24.left", {"start": v(2476.5, 69.14) * mm, "end": v(2476.5, -184.15) * mm});
            skLineSegment(sketch, "E24.right", {"start": v(5283.2, 69.14) * mm, "end": v(5283.2, -184.15) * mm});
            skSolve(sketch);
        }
        {
            var Q0;
            {var subQ1=makeQuery(id+"F16.opExtrude","SWEPT_FACE",FACE,{"disambiguationData":[OSD([sQuery(id+"F15.wireOp",EDGE,"E23.right")])]});var subQ2=makeQuery(id+"F5.opExtrude","SWEPT_FACE",FACE,{"disambiguationData":[OSD([sQuery(id+"F4.wireOp",EDGE,"E3.5.0.0")])]});var subQ3=makeQuery(id+"F16.boolean.opBoolean","INTERSECT",EDGE,{"derivedFrom":[subQ2,subQ1]});Q0=makeQuery(id+"F17.imprint","IMPRINT",FACE,{"disambiguationData":[TD([[makeQuery(id+"F17.imprint","IMPRINT",EDGE,{"derivedFrom":subQ3}),1.0]])]});}
            var Q1;
            {var subQ1=makeQuery(id+"F16.opExtrude","SWEPT_FACE",FACE,{"disambiguationData":[OSD([sQuery(id+"F15.wireOp",EDGE,"E23.right")])]});var subQ2=makeQuery(id+"F5.opExtrude","SWEPT_FACE",FACE,{"disambiguationData":[OSD([sQuery(id+"F4.wireOp",EDGE,"E3.5.0.1")])]});var subQ3=makeQuery(id+"F16.boolean.opBoolean","INTERSECT",EDGE,{"derivedFrom":[subQ2,subQ1]});Q1=makeQuery(id+"F17.imprint","IMPRINT",FACE,{"disambiguationData":[TD([[makeQuery(id+"F17.imprint","IMPRINT",EDGE,{"derivedFrom":subQ3}),-1.0]])]});}
            var Q2;
            {var subQ1=makeQuery(id+"F16.opExtrude","SWEPT_FACE",FACE,{"disambiguationData":[OSD([sQuery(id+"F15.wireOp",EDGE,"E23.right")])]});var subQ2=makeQuery(id+"F5.opExtrude","SWEPT_FACE",FACE,{"disambiguationData":[OSD([sQuery(id+"F4.wireOp",EDGE,"E3.6.0.1")])]});var subQ3=makeQuery(id+"F16.boolean.opBoolean","INTERSECT",EDGE,{"derivedFrom":[subQ2,subQ1]});Q2=makeQuery(id+"F17.imprint","IMPRINT",FACE,{"disambiguationData":[TD([[makeQuery(id+"F17.imprint","IMPRINT",EDGE,{"derivedFrom":subQ3}),-1.0]])]});}
            var Q3;
            {var subQ1=makeQuery(id+"F16.opExtrude","SWEPT_FACE",FACE,{"disambiguationData":[OSD([sQuery(id+"F15.wireOp",EDGE,"E23.right")])]});var subQ2=makeQuery(id+"F5.opExtrude","SWEPT_FACE",FACE,{"disambiguationData":[OSD([sQuery(id+"F4.wireOp",EDGE,"E3.7.0.1")])]});var subQ3=makeQuery(id+"F16.boolean.opBoolean","INTERSECT",EDGE,{"derivedFrom":[subQ2,subQ1]});Q3=makeQuery(id+"F17.imprint","IMPRINT",FACE,{"disambiguationData":[TD([[makeQuery(id+"F17.imprint","IMPRINT",EDGE,{"derivedFrom":subQ3}),-1.0]])]});}
            var Q4;
            {var subQ1=makeQuery(id+"F16.opExtrude","SWEPT_FACE",FACE,{"disambiguationData":[OSD([sQuery(id+"F15.wireOp",EDGE,"E23.right")])]});var subQ2=makeQuery(id+"F5.opExtrude","SWEPT_FACE",FACE,{"disambiguationData":[OSD([sQuery(id+"F4.wireOp",EDGE,"E3.8.0.1")])]});var subQ3=makeQuery(id+"F16.boolean.opBoolean","INTERSECT",EDGE,{"derivedFrom":[subQ2,subQ1]});Q4=makeQuery(id+"F17.imprint","IMPRINT",FACE,{"disambiguationData":[TD([[makeQuery(id+"F17.imprint","IMPRINT",EDGE,{"derivedFrom":subQ3}),-1.0]])]});}
            var Q5;
            {var subQ1=makeQuery(id+"F16.opExtrude","SWEPT_FACE",FACE,{"disambiguationData":[OSD([sQuery(id+"F15.wireOp",EDGE,"E23.right")])]});var subQ2=makeQuery(id+"F5.opExtrude","SWEPT_FACE",FACE,{"disambiguationData":[OSD([sQuery(id+"F4.wireOp",EDGE,"E3.9.0.1")])]});var subQ3=makeQuery(id+"F16.boolean.opBoolean","INTERSECT",EDGE,{"derivedFrom":[subQ2,subQ1]});Q5=makeQuery(id+"F17.imprint","IMPRINT",FACE,{"disambiguationData":[TD([[makeQuery(id+"F17.imprint","IMPRINT",EDGE,{"derivedFrom":subQ3}),-1.0]])]});}
            var Q6;
            {var subQ1=makeQuery(id+"F16.opExtrude","SWEPT_FACE",FACE,{"disambiguationData":[OSD([sQuery(id+"F15.wireOp",EDGE,"E23.right")])]});var subQ2=makeQuery(id+"F5.opExtrude","SWEPT_FACE",FACE,{"disambiguationData":[OSD([sQuery(id+"F4.wireOp",EDGE,"E3.10.0.1")])]});var subQ3=makeQuery(id+"F16.boolean.opBoolean","INTERSECT",EDGE,{"derivedFrom":[subQ2,subQ1]});Q6=makeQuery(id+"F17.imprint","IMPRINT",FACE,{"disambiguationData":[TD([[makeQuery(id+"F17.imprint","IMPRINT",EDGE,{"derivedFrom":subQ3}),-1.0]])]});}
            var Q7;
            {var subQ1=makeQuery(id+"F16.opExtrude","SWEPT_FACE",FACE,{"disambiguationData":[OSD([sQuery(id+"F15.wireOp",EDGE,"E23.right")])]});var subQ2=makeQuery(id+"F5.opExtrude","SWEPT_FACE",FACE,{"disambiguationData":[OSD([sQuery(id+"F4.wireOp",EDGE,"E3.11.0.1")])]});var subQ3=makeQuery(id+"F16.boolean.opBoolean","INTERSECT",EDGE,{"derivedFrom":[subQ2,subQ1]});Q7=makeQuery(id+"F17.imprint","IMPRINT",FACE,{"disambiguationData":[TD([[makeQuery(id+"F17.imprint","IMPRINT",EDGE,{"derivedFrom":subQ3}),-1.0]])]});}
            var Q8;
            {var subQ1=makeQuery(id+"F16.opExtrude","SWEPT_FACE",FACE,{"disambiguationData":[OSD([sQuery(id+"F15.wireOp",EDGE,"E23.right")])]});var subQ2=makeQuery(id+"F5.opExtrude","SWEPT_FACE",FACE,{"disambiguationData":[OSD([sQuery(id+"F4.wireOp",EDGE,"E3.6.0.0")])]});var subQ3=makeQuery(id+"F16.boolean.opBoolean","INTERSECT",EDGE,{"derivedFrom":[subQ2,subQ1]});Q8=makeQuery(id+"F17.imprint","IMPRINT",FACE,{"disambiguationData":[TD([[makeQuery(id+"F17.imprint","IMPRINT",EDGE,{"derivedFrom":subQ3}),1.0]])]});}
            extrude(context, id + "F18", {"entities" : qUnion([Q0, Q1, Q2, Q3, Q4, Q5, Q6, Q7, Q8]), "operationType" : NewBodyOperationType.ADD, "oppositeDirection" : true, "depth" : 38.1 * mm});
        }
        {
            var Q0;
            Q0=makeQuery(id+"F5.opExtrude","SWEPT_FACE",FACE,{"disambiguationData":[OSD([sQuery(id+"F4.wireOp",EDGE,"E3.12.0.1")])]});
            extrude(context, id + "F19", {"entities" : qUnion([Q0]), "operationType" : NewBodyOperationType.ADD, "depth" : 38.1 * mm});
        }
        {
            var Q0;
            Q0=makeQuery(id+"F5.opExtrude","SWEPT_FACE",FACE,{"disambiguationData":[OSD([sQuery(id+"F4.wireOp",EDGE,"E3.5.0.0")])]});
            extrude(context, id + "F20", {"entities" : qUnion([Q0]), "operationType" : NewBodyOperationType.ADD, "depth" : 38.1 * mm});
        }
        {
            var Q0;
            Q0=makeQuery(id+"F1.opExtrude","SWEPT_BODY",BODY,{"disambiguationData":[OSD([sQuery(id+"F0.wireOp",EDGE,"E0.bottom"),sQuery(id+"F0.wireOp",EDGE,"E0.top"),sQuery(id+"F0.wireOp",EDGE,"E0.left"),sQuery(id+"F0.wireOp",EDGE,"E0.right")])]});
            var Q1;
            Q1=qCreatedBy(makeId("Origin.pointOp"),VERTEX);
            transform(context, id + "F21", {"entities" : qUnion([Q0]), "transformType" : TransformType.SCALE_UNIFORMLY, "scale" : 1 / 87.1, "scalePoint" : qUnion([Q1]), "makeCopy" : false});
        }
    });
